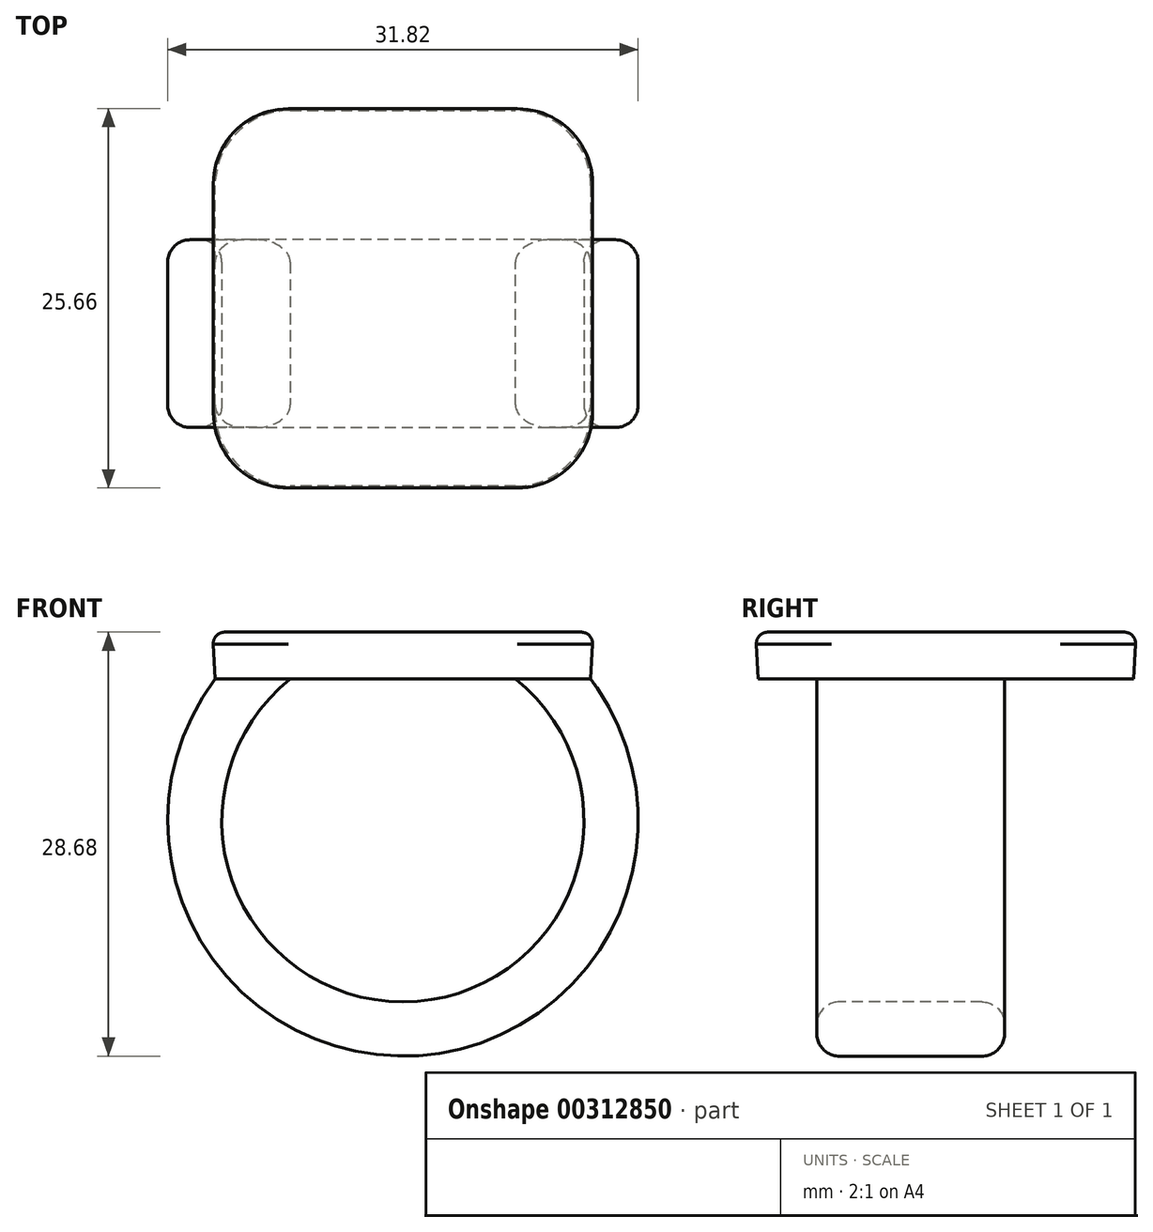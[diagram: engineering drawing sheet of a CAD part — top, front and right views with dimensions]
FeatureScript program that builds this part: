
annotation { "Feature Type Name" : "Feature", "Feature Type Description" : "" }
export const myFeature = defineFeature(function(context is Context, id is Id, definition is map)
    precondition{}
    {
        {
            var Q0;
            Q0=qCreatedBy(makeId("Top.planeOp"),FACE);
            var sketch = newSketch(context, id + "F0", { "sketchPlane" : qUnion([Q0])});
            skLineSegment(sketch, "E0.bottom", {"start": v(12.7, 12.7) * mm, "end": v(-12.7, 12.7) * mm});
            skLineSegment(sketch, "E0.top", {"start": v(12.7, -12.7) * mm, "end": v(-12.7, -12.7) * mm});
            skLineSegment(sketch, "E0.left", {"start": v(12.7, 12.7) * mm, "end": v(12.7, -12.7) * mm});
            skLineSegment(sketch, "E0.right", {"start": v(-12.7, 12.7) * mm, "end": v(-12.7, -12.7) * mm});
            skPoint(sketch, "E0.middle", {"position": v(0, 0) * mm});
            skSolve(sketch);
        }
        {
            var Q0;
            Q0 = qSketchRegion(id + "F0", true);
            extrude(context, id + "F1", {"entities" : qUnion([Q0]), "depth" : 3.17 * mm, "hasDraft" : true, "draftAngle" : 3 * degree});
        }
        {
            var Q0;
            Q0=qCreatedBy(makeId("Front.planeOp"),FACE);
            var sketch = newSketch(context, id + "F2", { "sketchPlane" : qUnion([Q0])});
            skArc(sketch, "E1", {"start": v(-10.16, 0) * mm, "mid": v(0, -23.56) * mm, "end": v(10.16, 0) * mm});
            skSolve(sketch);
        }
        {
            var Q0;
            Q0=makeQuery(id+"F1.opExtrude","CAP_FACE",FACE,{"disambiguationData":[OSD([sQuery(id+"F0.wireOp",EDGE,"E0.bottom"),sQuery(id+"F0.wireOp",EDGE,"E0.top"),sQuery(id+"F0.wireOp",EDGE,"E0.left"),sQuery(id+"F0.wireOp",EDGE,"E0.right")])],"isStart":true});
            var sketch = newSketch(context, id + "F3", { "sketchPlane" : qUnion([Q0])});
            skLineSegment(sketch, "E2.bottom", {"start": v(-7.62, -3.96) * mm, "end": v(-12.7, -3.96) * mm});
            skLineSegment(sketch, "E2.top", {"start": v(-7.62, 8.74) * mm, "end": v(-12.7, 8.74) * mm});
            skLineSegment(sketch, "E2.left", {"start": v(-7.62, -3.96) * mm, "end": v(-7.62, 8.74) * mm});
            skLineSegment(sketch, "E2.right", {"start": v(-12.7, -3.96) * mm, "end": v(-12.7, 8.74) * mm});
            skPoint(sketch, "E2.middle", {"position": v(-10.16, 2.4) * mm});
            skSolve(sketch);
        }
        {
            var Q0;
            Q0 = qSketchRegion(id + "F3", true);
            var Q1;
            Q1 = qConstructionFilter(qBodyType(qCreatedBy(id + "F2" ,EDGE), BodyType.WIRE), ConstructionObject.NO);
            sweep(context, id + "F4", {"operationType" : NewBodyOperationType.ADD, "profiles" : qUnion([Q0]), "path" : qUnion([Q1])});
        }
        {
            var Q0;
            Q0=qCreatedBy(makeId("Front.planeOp"),FACE);
            var sketch = newSketch(context, id + "F5", { "sketchPlane" : qUnion([Q0])});
            skLineSegment(sketch, "E3.0", {"start": v(10.16, 0) * mm, "end": v(7.62, 0) * mm});
            skLineSegment(sketch, "E4.1", {"start": v(10.01, -2.54) * mm, "end": v(10.16, 0) * mm});
            skArc(sketch, "E4.2", {"start": v(10.01, -2.54) * mm, "mid": v(8.9, -1.18) * mm, "end": v(7.62, 0) * mm});
            skPoint(sketch, "E5.trimOffspring.end.orphan", {"position": v(-12.7, 0) * mm});
            skPoint(sketch, "E6.orphan", {"position": v(-7.62, 0) * mm});
            skPoint(sketch, "E7.orphan", {"position": v(12.7, 0) * mm});
            skSolve(sketch);
        }
        {
            var Q0;
            Q0 = qSketchRegion(id + "F5", true);
            var Q1;
            Q1=makeQuery(id+"F4.opSweep","SWEPT_FACE",FACE,{"disambiguationData":[OSD([sQuery(id+"F2.wireOp",EDGE,"E1"),sQuery(id+"F3.wireOp",EDGE,"E2.top")])]});
            var Q2;
            Q2=makeQuery(id+"F4.opSweep","SWEPT_FACE",FACE,{"disambiguationData":[OSD([sQuery(id+"F2.wireOp",EDGE,"E1"),sQuery(id+"F3.wireOp",EDGE,"E2.bottom")])]});
            extrude(context, id + "F6", {"entities" : qUnion([Q0]), "operationType" : NewBodyOperationType.ADD, "endBound" : BoundingType.UP_TO_SURFACE, "endBoundEntityFace" : qUnion([Q1]), "depth" : 25.4 * mm, "hasSecondDirection" : true, "secondDirectionBound" : SecondDirectionBoundingType.UP_TO_SURFACE, "secondDirectionOppositeDirection" : true, "secondDirectionBoundEntityFace" : qUnion([Q2]), "secondDirectionDepth" : 25.4 * mm});
        }
        {
            var Q0;
            Q0=makeQuery(id+"F1.opExtrude","SWEPT_EDGE",EDGE,{"disambiguationData":[OSD([sQuery(id+"F0.wireOp",EDGE,"E0.top"),sQuery(id+"F0.wireOp",EDGE,"E0.right")])]});
            var Q1;
            Q1=makeQuery(id+"F1.opExtrude","SWEPT_EDGE",EDGE,{"disambiguationData":[OSD([sQuery(id+"F0.wireOp",EDGE,"E0.top"),sQuery(id+"F0.wireOp",EDGE,"E0.left")])]});
            var Q2;
            Q2=makeQuery(id+"F1.opExtrude","SWEPT_EDGE",EDGE,{"disambiguationData":[OSD([sQuery(id+"F0.wireOp",EDGE,"E0.bottom"),sQuery(id+"F0.wireOp",EDGE,"E0.left")])]});
            var Q3;
            Q3=makeQuery(id+"F1.opExtrude","SWEPT_EDGE",EDGE,{"disambiguationData":[OSD([sQuery(id+"F0.wireOp",EDGE,"E0.bottom"),sQuery(id+"F0.wireOp",EDGE,"E0.right")])]});
            fillet(context, id + "F7", {"entities" : qUnion([Q0, Q1, Q2, Q3]), "radius" : 5.08 * mm, "tangentPropagation" : true, "allowEdgeOverflow" : false});
        }
        {
            var Q0;
            Q0=makeQuery(id+"F4.opSweep","SWEPT_EDGE",EDGE,{"disambiguationData":[OSD([sQuery(id+"F0.wireOp",EDGE,"E0.right"),sQuery(id+"F2.wireOp",EDGE,"E1"),sQuery(id+"F3.wireOp",EDGE,"E2.top"),sQuery(id+"F3.wireOp",EDGE,"E2.right")])]});
            var Q1;
            {var subQ0=sQuery(id+"F3.wireOp",EDGE,"E2.top");var subQ1=sQuery(id+"F2.wireOp",EDGE,"E1");Q1=makeQuery(id+"F6.boolean.opBoolean","MERGE",EDGE,{"derivedFrom":[makeQuery(id+"F4.opSweep","SWEPT_EDGE",EDGE,{"disambiguationData":[OSD([subQ1,subQ0,sQuery(id+"F3.wireOp",EDGE,"E2.left")])]}),makeQuery(id+"F6.opExtrude","TWEAK_EDGE",EDGE,{"derivedFrom":[makeQuery(id+"F4.opSweep","SWEPT_FACE",FACE,{"disambiguationData":[OSD([subQ1,subQ0])]}),makeQuery(id+"F5.imprint","IMPRINT",EDGE,{"derivedFrom":sQuery(id+"F5.wireOp",EDGE,"E4.2")})]})]});}
            var Q2;
            {var subQ0=sQuery(id+"F3.wireOp",EDGE,"E2.bottom");var subQ1=sQuery(id+"F2.wireOp",EDGE,"E1");Q2=makeQuery(id+"F6.boolean.opBoolean","MERGE",EDGE,{"derivedFrom":[makeQuery(id+"F4.opSweep","SWEPT_EDGE",EDGE,{"disambiguationData":[OSD([subQ1,subQ0,sQuery(id+"F3.wireOp",EDGE,"E2.left")])]}),makeQuery(id+"F6.opExtrude","TWEAK_EDGE",EDGE,{"derivedFrom":[makeQuery(id+"F4.opSweep","SWEPT_FACE",FACE,{"disambiguationData":[OSD([subQ1,subQ0])]}),makeQuery(id+"F5.imprint","IMPRINT",EDGE,{"derivedFrom":sQuery(id+"F5.wireOp",EDGE,"E4.2")})]})]});}
            var Q3;
            Q3=makeQuery(id+"F4.opSweep","SWEPT_EDGE",EDGE,{"disambiguationData":[OSD([sQuery(id+"F0.wireOp",EDGE,"E0.right"),sQuery(id+"F2.wireOp",EDGE,"E1"),sQuery(id+"F3.wireOp",EDGE,"E2.bottom"),sQuery(id+"F3.wireOp",EDGE,"E2.right")])]});
            fillet(context, id + "F8", {"entities" : qUnion([Q0, Q1, Q2, Q3]), "radius" : 1.52 * mm, "tangentPropagation" : true, "allowEdgeOverflow" : false});
        }
        {
            var Q0;
            Q0=makeQuery(id+"F1.opExtrude","CAP_FACE",FACE,{"disambiguationData":[OSD([sQuery(id+"F0.wireOp",EDGE,"E0.bottom"),sQuery(id+"F0.wireOp",EDGE,"E0.top"),sQuery(id+"F0.wireOp",EDGE,"E0.left"),sQuery(id+"F0.wireOp",EDGE,"E0.right")])],"isStart":false});
            fillet(context, id + "F9", {"entities" : qUnion([Q0]), "radius" : 0.76 * mm, "tangentPropagation" : true, "allowEdgeOverflow" : false});
        }
    });
